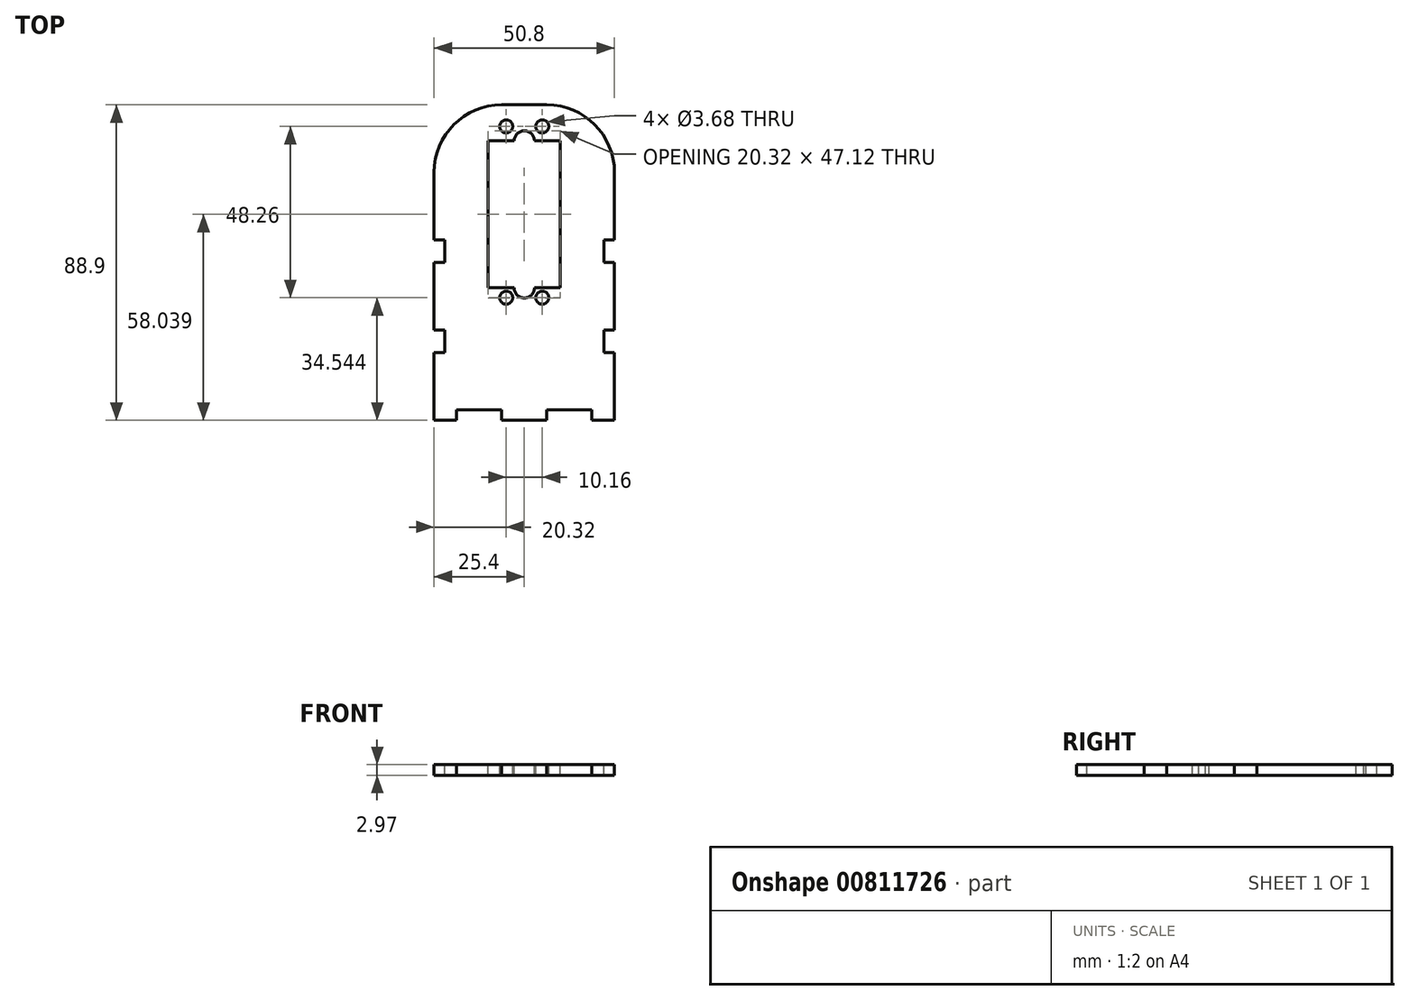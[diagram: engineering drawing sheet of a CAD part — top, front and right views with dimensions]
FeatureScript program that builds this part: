
annotation { "Feature Type Name" : "Feature", "Feature Type Description" : "" }
export const myFeature = defineFeature(function(context is Context, id is Id, definition is map)
    precondition{}
    {
        {
            var Q0;
            Q0=qCreatedBy(makeId("Top.planeOp"),FACE);
            var sketch = newSketch(context, id + "F0", { "sketchPlane" : qUnion([Q0])});
            skLineSegment(sketch, "E0.bottom", {"start": v(25.4, 44.45) * mm, "end": v(-25.4, 44.45) * mm});
            skLineSegment(sketch, "E0.top", {"start": v(25.4, -44.45) * mm, "end": v(-25.4, -44.45) * mm});
            skLineSegment(sketch, "E0.left", {"start": v(25.4, 44.45) * mm, "end": v(25.4, -44.45) * mm});
            skLineSegment(sketch, "E0.right", {"start": v(-25.4, 44.45) * mm, "end": v(-25.4, -44.45) * mm});
            skPoint(sketch, "E0.middle", {"position": v(0, 0) * mm});
            skSolve(sketch);
        }
        {
            var Q0;
            Q0 = qSketchRegion(id + "F0", true);
            extrude(context, id + "F1", {"entities" : qUnion([Q0]), "depth" : 2.97 * mm, "offsetDistance" : 25.4 * mm});
        }
        {
            var Q0;
            Q0=makeQuery(id+"F1.opExtrude","CAP_FACE",FACE,{"disambiguationData":[OSD([sQuery(id+"F0.wireOp",EDGE,"E0.bottom"),sQuery(id+"F0.wireOp",EDGE,"E0.top"),sQuery(id+"F0.wireOp",EDGE,"E0.left"),sQuery(id+"F0.wireOp",EDGE,"E0.right")])],"isStart":false});
            var sketch = newSketch(context, id + "F2", { "sketchPlane" : qUnion([Q0])});
            skLineSegment(sketch, "E1.bottom", {"start": v(10.16, -7.11) * mm, "end": v(-10.16, -7.11) * mm});
            skLineSegment(sketch, "E1.top", {"start": v(10.16, 34.3) * mm, "end": v(-10.16, 34.3) * mm});
            skLineSegment(sketch, "E1.left", {"start": v(10.16, -7.11) * mm, "end": v(10.16, 34.3) * mm});
            skLineSegment(sketch, "E1.right", {"start": v(-10.16, -7.11) * mm, "end": v(-10.16, 34.3) * mm});
            skPoint(sketch, "E1.middle", {"position": v(0, 13.59) * mm});
            skSolve(sketch);
        }
        {
            var Q0;
            Q0 = qSketchRegion(id + "F2", true);
            extrude(context, id + "F3", {"entities" : qUnion([Q0]), "operationType" : NewBodyOperationType.REMOVE, "oppositeDirection" : true, "depth" : 25.4 * mm, "offsetDistance" : 25.4 * mm});
        }
        {
            var Q0;
            Q0=makeQuery(id+"F1.opExtrude","CAP_FACE",FACE,{"disambiguationData":[OSD([sQuery(id+"F0.wireOp",EDGE,"E0.bottom"),sQuery(id+"F0.wireOp",EDGE,"E0.top"),sQuery(id+"F0.wireOp",EDGE,"E0.left"),sQuery(id+"F0.wireOp",EDGE,"E0.right")])],"isStart":false});
            var sketch = newSketch(context, id + "F4", { "sketchPlane" : qUnion([Q0])});
            skLineSegment(sketch, "E2.bottom", {"start": v(-19.05, -44.45) * mm, "end": v(-6.35, -44.45) * mm});
            skLineSegment(sketch, "E2.top", {"start": v(-19.05, -41.48) * mm, "end": v(-6.35, -41.48) * mm});
            skLineSegment(sketch, "E2.left", {"start": v(-19.05, -44.45) * mm, "end": v(-19.05, -41.48) * mm});
            skLineSegment(sketch, "E2.right", {"start": v(-6.35, -44.45) * mm, "end": v(-6.35, -41.48) * mm});
            skLineSegment(sketch, "E3.bottom", {"start": v(6.35, -44.45) * mm, "end": v(19.05, -44.45) * mm});
            skLineSegment(sketch, "E3.top", {"start": v(6.35, -41.48) * mm, "end": v(19.05, -41.48) * mm});
            skLineSegment(sketch, "E3.left", {"start": v(6.35, -44.45) * mm, "end": v(6.35, -41.48) * mm});
            skLineSegment(sketch, "E3.right", {"start": v(19.05, -44.45) * mm, "end": v(19.05, -41.48) * mm});
            skSolve(sketch);
        }
        {
            var Q0;
            Q0 = qSketchRegion(id + "F4", true);
            extrude(context, id + "F5", {"entities" : qUnion([Q0]), "operationType" : NewBodyOperationType.REMOVE, "oppositeDirection" : true, "depth" : 25.4 * mm, "offsetDistance" : 25.4 * mm});
        }
        {
            var Q0;
            Q0=makeQuery(id+"F1.opExtrude","CAP_FACE",FACE,{"disambiguationData":[OSD([sQuery(id+"F0.wireOp",EDGE,"E0.bottom"),sQuery(id+"F0.wireOp",EDGE,"E0.top"),sQuery(id+"F0.wireOp",EDGE,"E0.left"),sQuery(id+"F0.wireOp",EDGE,"E0.right")])],"isStart":false});
            var sketch = newSketch(context, id + "F6", { "sketchPlane" : qUnion([Q0])});
            skLineSegment(sketch, "E4.bottom", {"start": v(25.4, 6.35) * mm, "end": v(22.43, 6.35) * mm});
            skLineSegment(sketch, "E4.top", {"start": v(25.4, 0) * mm, "end": v(22.43, 0) * mm});
            skLineSegment(sketch, "E4.left", {"start": v(25.4, 6.35) * mm, "end": v(25.4, 0) * mm});
            skLineSegment(sketch, "E4.right", {"start": v(22.43, 6.35) * mm, "end": v(22.43, 0) * mm});
            skLineSegment(sketch, "E5.bottom", {"start": v(-25.4, 6.35) * mm, "end": v(-22.43, 6.35) * mm});
            skLineSegment(sketch, "E5.top", {"start": v(-25.4, 0) * mm, "end": v(-22.43, 0) * mm});
            skLineSegment(sketch, "E5.left", {"start": v(-25.4, 6.35) * mm, "end": v(-25.4, 0) * mm});
            skLineSegment(sketch, "E5.right", {"start": v(-22.43, 6.35) * mm, "end": v(-22.43, 0) * mm});
            skLineSegment(sketch, "E6.bottom", {"start": v(-25.4, -19.05) * mm, "end": v(-22.43, -19.05) * mm});
            skLineSegment(sketch, "E6.top", {"start": v(-25.4, -25.4) * mm, "end": v(-22.43, -25.4) * mm});
            skLineSegment(sketch, "E6.left", {"start": v(-25.4, -19.05) * mm, "end": v(-25.4, -25.4) * mm});
            skLineSegment(sketch, "E6.right", {"start": v(-22.43, -19.05) * mm, "end": v(-22.43, -25.4) * mm});
            skLineSegment(sketch, "E7.bottom", {"start": v(25.4, -19.05) * mm, "end": v(22.43, -19.05) * mm});
            skLineSegment(sketch, "E7.top", {"start": v(25.4, -25.4) * mm, "end": v(22.43, -25.4) * mm});
            skLineSegment(sketch, "E7.left", {"start": v(25.4, -19.05) * mm, "end": v(25.4, -25.4) * mm});
            skLineSegment(sketch, "E7.right", {"start": v(22.43, -19.05) * mm, "end": v(22.43, -25.4) * mm});
            skSolve(sketch);
        }
        {
            var Q0;
            Q0 = qSketchRegion(id + "F6", true);
            extrude(context, id + "F7", {"entities" : qUnion([Q0]), "operationType" : NewBodyOperationType.REMOVE, "oppositeDirection" : true, "depth" : 25.4 * mm, "offsetDistance" : 25.4 * mm});
        }
        {
            var Q0;
            Q0=makeQuery(id+"F1.opExtrude","CAP_FACE",FACE,{"disambiguationData":[OSD([sQuery(id+"F0.wireOp",EDGE,"E0.bottom"),sQuery(id+"F0.wireOp",EDGE,"E0.top"),sQuery(id+"F0.wireOp",EDGE,"E0.left"),sQuery(id+"F0.wireOp",EDGE,"E0.right")])],"isStart":false});
            var sketch = newSketch(context, id + "F8", { "sketchPlane" : qUnion([Q0])});
            skCircle(sketch, "E8", {"center": v(-5.08, 38.35) * mm, "radius": 1.84 * mm});
            skCircle(sketch, "E9", {"center": v(5.08, 38.35) * mm, "radius": 1.84 * mm});
            skCircle(sketch, "E10", {"center": v(-5.08, -9.9) * mm, "radius": 1.84 * mm});
            skCircle(sketch, "E11", {"center": v(5.08, -9.9) * mm, "radius": 1.84 * mm});
            skSolve(sketch);
        }
        {
            var Q0;
            Q0 = qSketchRegion(id + "F8", true);
            extrude(context, id + "F9", {"entities" : qUnion([Q0]), "operationType" : NewBodyOperationType.REMOVE, "oppositeDirection" : true, "depth" : 25.4 * mm, "offsetDistance" : 25.4 * mm});
        }
        {
            var Q0;
            Q0=makeQuery(id+"F1.opExtrude","CAP_FACE",FACE,{"disambiguationData":[OSD([sQuery(id+"F0.wireOp",EDGE,"E0.bottom"),sQuery(id+"F0.wireOp",EDGE,"E0.top"),sQuery(id+"F0.wireOp",EDGE,"E0.left"),sQuery(id+"F0.wireOp",EDGE,"E0.right")])],"isStart":false});
            var sketch = newSketch(context, id + "F10", { "sketchPlane" : qUnion([Q0])});
            skArc(sketch, "E12", {"start": v(-2.86, 34.3) * mm, "mid": v(0, 37.15) * mm, "end": v(2.86, 34.3) * mm});
            skLineSegment(sketch, "E13", {"start": v(-2.86, 34.3) * mm, "end": v(2.86, 34.3) * mm});
            skArc(sketch, "E14", {"start": v(2.86, -7.11) * mm, "mid": v(0, -9.97) * mm, "end": v(-2.86, -7.11) * mm});
            skLineSegment(sketch, "E15", {"start": v(-2.86, -7.11) * mm, "end": v(2.86, -7.11) * mm});
            skSolve(sketch);
        }
        {
            var Q0;
            Q0 = qSketchRegion(id + "F10", true);
            extrude(context, id + "F11", {"entities" : qUnion([Q0]), "operationType" : NewBodyOperationType.REMOVE, "oppositeDirection" : true, "depth" : 25.4 * mm, "offsetDistance" : 25.4 * mm});
        }
        {
            var Q0;
            Q0=makeQuery(id+"F1.opExtrude","SWEPT_EDGE",EDGE,{"disambiguationData":[OSD([sQuery(id+"F0.wireOp",EDGE,"E0.bottom"),sQuery(id+"F0.wireOp",EDGE,"E0.left")])]});
            var Q1;
            Q1=makeQuery(id+"F1.opExtrude","SWEPT_EDGE",EDGE,{"disambiguationData":[OSD([sQuery(id+"F0.wireOp",EDGE,"E0.bottom"),sQuery(id+"F0.wireOp",EDGE,"E0.right")])]});
            fillet(context, id + "F12", {"entities" : qUnion([Q0, Q1]), "radius" : 19.05 * mm, "tangentPropagation" : true, "allowEdgeOverflow" : false});
        }
    });
